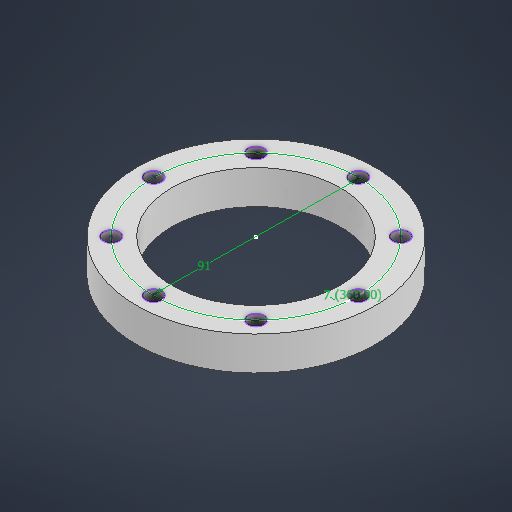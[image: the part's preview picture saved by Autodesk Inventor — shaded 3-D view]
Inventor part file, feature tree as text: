
AUTODESK INVENTOR PART (.ipt)
format: ipt  version: 2025 (Build 290162000, 162)  size: 249,856 bytes
history: native  units: in
note: dims shown in document units (in); Inventor stores cm internally (conversion verified against a paired STEP export)
features: sketch x5, extrude x3
ambient origin geometry x8: Origin, YZ Plane, XZ Plane, XY Plane, X Axis, Y Axis, Z Axis, Center Point
bodies: Solid1 (feature_tree)
feature tree (8):
  extrude  "Extrusion1"  Depth=2.9528in
  extrude  "Extrusion2"  Depth=0.5906in
  extrude  "Extrusion3"  Depth=0.1969in TaperAngle=360.0deg
  sketch  "Sketch1"  dims[d0=4.1831in d1=2.9528in]
  sketch  "Sketch2"  dims[d5=0.1969in d6=3.1496in d8=360.0deg]
  sketch  "Sketch Circular Pattern1"  dims[d2=0.5906in d3=0.0in d4=3.248in]
  sketch  "Sketch3"  dims[d12=3.5827in d13=0.2756in d14=3.1496in d16=360.0deg d18=0.2756in d19=0.0in]
  sketch  "Sketch Circular Pattern2"  dims[d10=0.1181in d11=0.0in]
